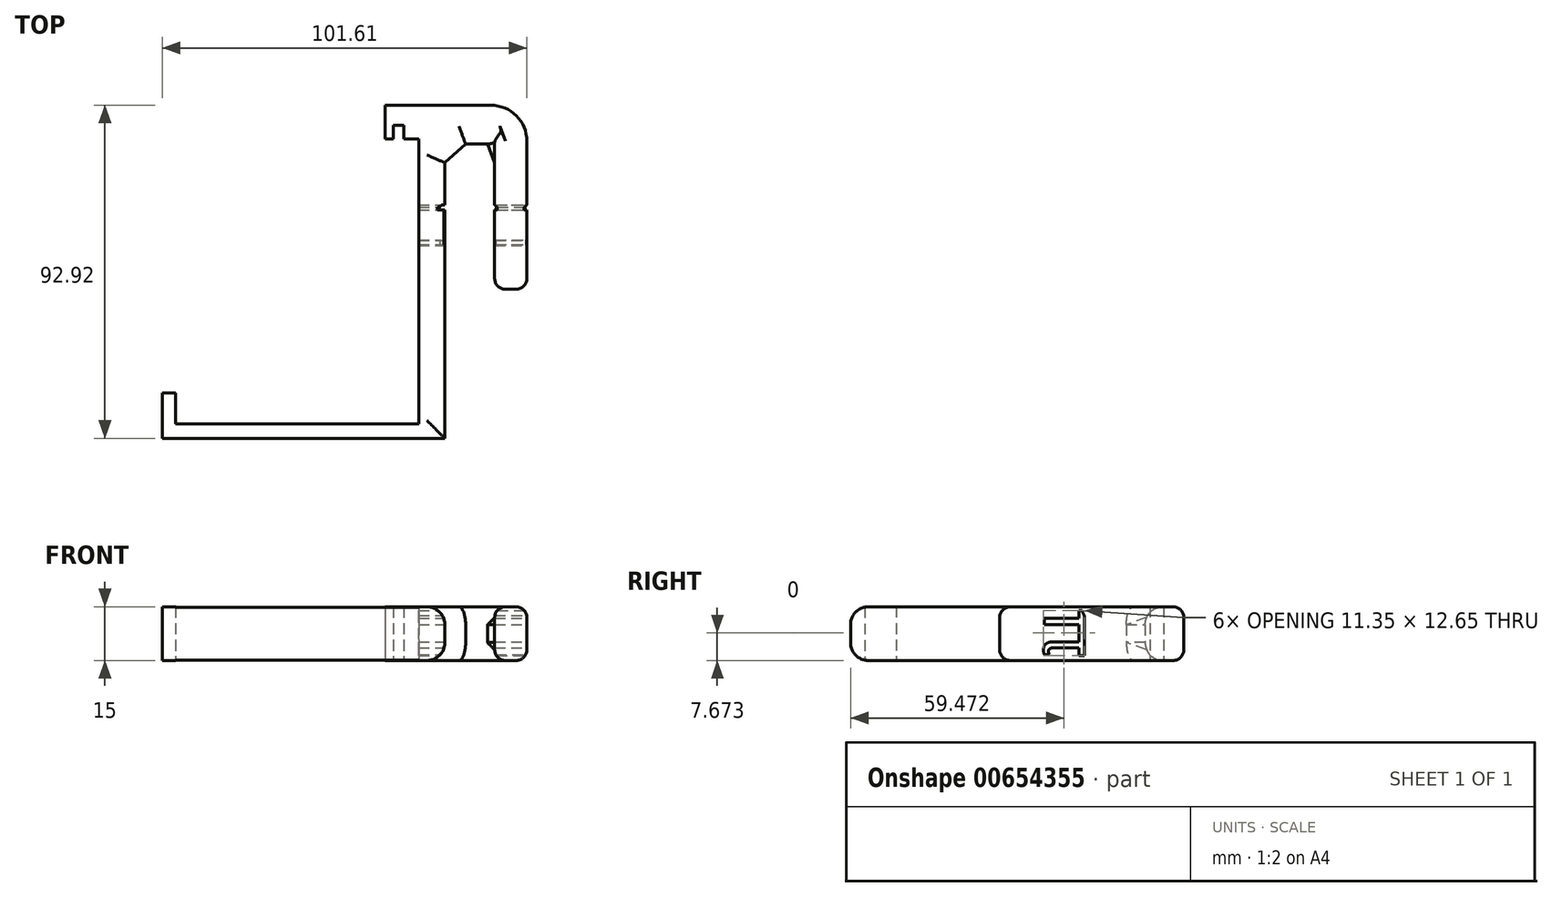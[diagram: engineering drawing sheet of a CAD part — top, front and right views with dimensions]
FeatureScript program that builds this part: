
annotation { "Feature Type Name" : "Feature", "Feature Type Description" : "" }
export const myFeature = defineFeature(function(context is Context, id is Id, definition is map)
    precondition{}
    {
        {
            var Q0;
            Q0=qCreatedBy(makeId("Top.planeOp"),FACE);
            var sketch = newSketch(context, id + "F0", { "sketchPlane" : qUnion([Q0])});
            skLineSegment(sketch, "E0", {"start": v(-34.84, -32.24) * mm, "end": v(31.61, -32.24) * mm});
            skLineSegment(sketch, "E1", {"start": v(31.61, -32.24) * mm, "end": v(31.61, 47.34) * mm});
            skLineSegment(sketch, "E2", {"start": v(31.61, 47.34) * mm, "end": v(27.45, 47.34) * mm});
            skLineSegment(sketch, "E3", {"start": v(27.45, 47.34) * mm, "end": v(27.45, 51.1) * mm});
            skLineSegment(sketch, "E4", {"start": v(27.45, 51.1) * mm, "end": v(24.53, 51.1) * mm});
            skLineSegment(sketch, "E5", {"start": v(24.53, 51.1) * mm, "end": v(24.53, 47.34) * mm});
            skLineSegment(sketch, "E6", {"start": v(24.53, 47.34) * mm, "end": v(22.24, 47.34) * mm});
            skLineSegment(sketch, "E7", {"start": v(22.24, 47.34) * mm, "end": v(22.24, 56.72) * mm});
            skLineSegment(sketch, "E8", {"start": v(22.24, 56.72) * mm, "end": v(38.9, 56.72) * mm});
            skLineSegment(sketch, "E9", {"start": v(38.9, 56.72) * mm, "end": v(38.9, -36.2) * mm});
            skLineSegment(sketch, "E10", {"start": v(38.9, -36.2) * mm, "end": v(-39.84, -36.2) * mm});
            skLineSegment(sketch, "E11", {"start": v(-39.84, -36.2) * mm, "end": v(-39.84, -23.49) * mm});
            skLineSegment(sketch, "E12", {"start": v(-39.84, -23.49) * mm, "end": v(-36.1, -23.49) * mm});
            skLineSegment(sketch, "E13", {"start": v(-36.1, -23.49) * mm, "end": v(-36.1, -32.24) * mm});
            skLineSegment(sketch, "E14", {"start": v(-36.1, -32.24) * mm, "end": v(-34.84, -32.24) * mm});
            skLineSegment(sketch, "E15", {"start": v(38.9, 40.67) * mm, "end": v(44.71, 45.93) * mm});
            skLineSegment(sketch, "E16", {"start": v(44.71, 45.93) * mm, "end": v(50.79, 45.93) * mm});
            skLineSegment(sketch, "E17", {"start": v(50.79, 45.93) * mm, "end": v(52.8, 40.67) * mm});
            skLineSegment(sketch, "E18", {"start": v(52.8, 40.67) * mm, "end": v(52.8, 5.37) * mm});
            skLineSegment(sketch, "E19", {"start": v(52.8, 5.37) * mm, "end": v(61.77, 5.37) * mm});
            skLineSegment(sketch, "E20", {"start": v(61.77, 5.37) * mm, "end": v(61.77, 56.72) * mm});
            skLineSegment(sketch, "E21", {"start": v(61.77, 56.72) * mm, "end": v(38.9, 56.72) * mm});
            skSolve(sketch);
        }
        {
            var Q0;
            Q0=makeQuery(id+"F0.imprint","IMPRINT",FACE,{"disambiguationData":[TD([[makeQuery(id+"F0.imprint","IMPRINT",EDGE,{"derivedFrom":sQuery(id+"F0.wireOp",EDGE,"E0")}),-1.0]])]});
            var Q1;
            {var subQ0=sQuery(id+"F0.wireOp",EDGE,"f9ffd797-5b7e-4a78-90b0-e5bad0ac81ea");Q1=makeQuery(id+"F0.imprint","IMPRINT",FACE,{"disambiguationData":[TD([[makeQuery(id+"F0.imprint","IMPRINT",EDGE,{"derivedFrom":subQ0}),-1.0]])]});}
            var Q2;
            {var subQ0=sQuery(id+"F0.wireOp",EDGE,"E15");Q2=makeQuery(id+"F0.imprint","IMPRINT",FACE,{"disambiguationData":[TD([[makeQuery(id+"F0.imprint","IMPRINT",EDGE,{"derivedFrom":subQ0}),1.0]])]});}
            extrude(context, id + "F1", {"entities" : qUnion([Q0, Q1, Q2]), "depth" : 15 * mm, "offsetDistance" : 25 * mm});
        }
        {
            var Q0;
            Q0=makeQuery(id+"F1.opExtrude","SWEPT_EDGE",EDGE,{"disambiguationData":[OSD([sQuery(id+"F0.wireOp",EDGE,"E20"),sQuery(id+"F0.wireOp",EDGE,"E21")])]});
            fillet(context, id + "F2", {"entities" : qUnion([Q0]), "radius" : 10 * mm, "tangentPropagation" : true, "allowEdgeOverflow" : false});
        }
        {
            var Q0;
            Q0=makeQuery(id+"F1.opExtrude","SWEPT_FACE",FACE,{"disambiguationData":[OSD([sQuery(id+"F0.wireOp",EDGE,"E20")])]});
            var sketch = newSketch(context, id + "F3", { "sketchPlane" : qUnion([Q0])});
            skText(sketch, "E22", { "text": "π", "fontName": "OpenSans-Regular.ttf"});
            const initialGuessF3  = {"E22": [0.0178, 0.01425, 0, -1, 0.015]};
            skSetInitialGuess(sketch, initialGuessF3);
            skSolve(sketch);
        }
        {
            var Q0;
            Q0 = qSketchRegion(id + "F3", true);
            extrude(context, id + "F4", {"entities" : qUnion([Q0]), "operationType" : NewBodyOperationType.REMOVE, "oppositeDirection" : true, "depth" : 35 * mm, "offsetDistance" : 25 * mm});
        }
        {
            var Q0;
            Q0=makeQuery(id+"F1.opExtrude","SWEPT_EDGE",EDGE,{"disambiguationData":[OSD([sQuery(id+"F0.wireOp",EDGE,"E19"),sQuery(id+"F0.wireOp",EDGE,"E20")])]});
            var Q1;
            Q1=makeQuery(id+"F1.opExtrude","SWEPT_EDGE",EDGE,{"disambiguationData":[OSD([sQuery(id+"F0.wireOp",EDGE,"E18"),sQuery(id+"F0.wireOp",EDGE,"E19")])]});
            fillet(context, id + "F5", {"entities" : qUnion([Q0, Q1]), "radius" : 3 * mm, "tangentPropagation" : true, "allowEdgeOverflow" : false});
        }
        {
            var Q0;
            Q0=makeQuery(id+"F1.opExtrude","CAP_EDGE",EDGE,{"disambiguationData":[OSD([sQuery(id+"F0.wireOp",EDGE,"E9")])],"isStart":false});
            var Q1;
            Q1=makeQuery(id+"F1.opExtrude","CAP_EDGE",EDGE,{"disambiguationData":[OSD([sQuery(id+"F0.wireOp",EDGE,"E9")])],"isStart":true});
            var Q2;
            Q2=makeQuery(id+"F1.opExtrude","CAP_EDGE",EDGE,{"disambiguationData":[OSD([sQuery(id+"F0.wireOp",EDGE,"E10")])],"isStart":false});
            var Q3;
            Q3=makeQuery(id+"F1.opExtrude","CAP_EDGE",EDGE,{"disambiguationData":[OSD([sQuery(id+"F0.wireOp",EDGE,"E10")])],"isStart":true});
            fillet(context, id + "F6", {"entities" : qUnion([Q0, Q1, Q2, Q3]), "radius" : 5 * mm, "tangentPropagation" : true, "allowEdgeOverflow" : false});
        }
        {
            var Q0;
            Q0=makeQuery(id+"F1.opExtrude","CAP_EDGE",EDGE,{"disambiguationData":[OSD([sQuery(id+"F0.wireOp",EDGE,"E8"),sQuery(id+"F0.wireOp",EDGE,"E21")])],"isStart":false});
            var Q1;
            Q1=makeQuery(id+"F1.opExtrude","CAP_EDGE",EDGE,{"disambiguationData":[OSD([sQuery(id+"F0.wireOp",EDGE,"E8"),sQuery(id+"F0.wireOp",EDGE,"E21")])],"isStart":true});
            fillet(context, id + "F7", {"entities" : qUnion([Q0, Q1]), "radius" : 3 * mm, "tangentPropagation" : true, "allowEdgeOverflow" : false});
        }
        {
            var Q0;
            Q0=makeQuery(id+"F1.opExtrude","CAP_EDGE",EDGE,{"disambiguationData":[OSD([sQuery(id+"F0.wireOp",EDGE,"E15")])],"isStart":false});
            var Q1;
            Q1=makeQuery(id+"F1.opExtrude","CAP_EDGE",EDGE,{"disambiguationData":[OSD([sQuery(id+"F0.wireOp",EDGE,"E16")])],"isStart":false});
            var Q2;
            Q2=makeQuery(id+"F1.opExtrude","CAP_EDGE",EDGE,{"disambiguationData":[OSD([sQuery(id+"F0.wireOp",EDGE,"E15")])],"isStart":true});
            var Q3;
            Q3=makeQuery(id+"F1.opExtrude","CAP_EDGE",EDGE,{"disambiguationData":[OSD([sQuery(id+"F0.wireOp",EDGE,"E16")])],"isStart":true});
            fillet(context, id + "F8", {"entities" : qUnion([Q0, Q1, Q2, Q3]), "radius" : 5 * mm, "tangentPropagation" : true, "allowEdgeOverflow" : false});
        }
        {
            var Q0;
            Q0=makeQuery(id+"F1.opExtrude","CAP_EDGE",EDGE,{"disambiguationData":[OSD([sQuery(id+"F0.wireOp",EDGE,"E17")])],"isStart":false});
            var Q1;
            Q1=makeQuery(id+"F1.opExtrude","CAP_EDGE",EDGE,{"disambiguationData":[OSD([sQuery(id+"F0.wireOp",EDGE,"E17")])],"isStart":true});
            chamfer(context, id + "F9", {"entities" : qUnion([Q0, Q1]), "width" : 5 * mm, "tangentPropagation" : true});
        }
    });
